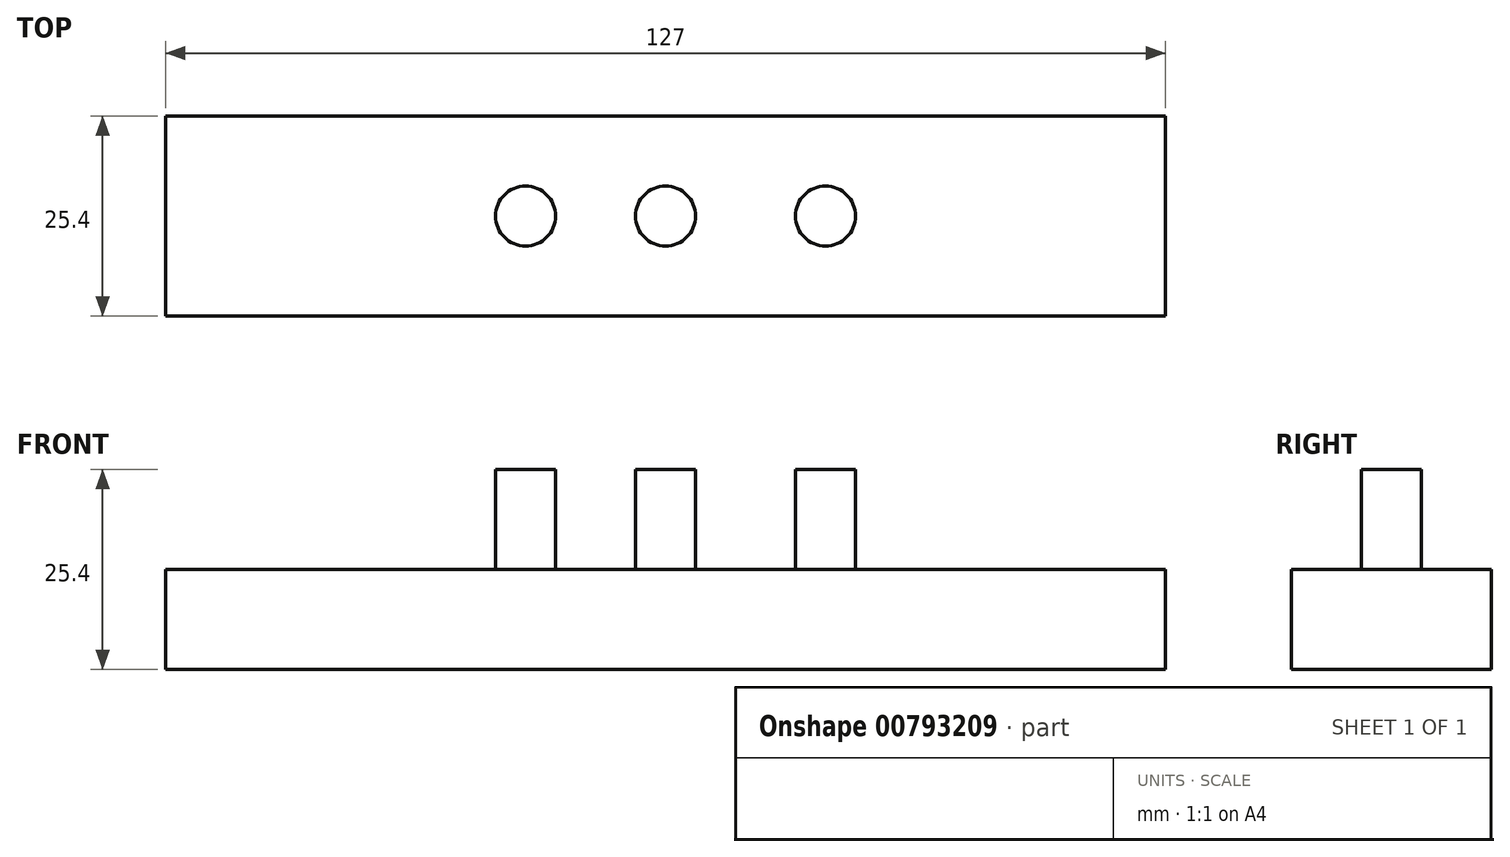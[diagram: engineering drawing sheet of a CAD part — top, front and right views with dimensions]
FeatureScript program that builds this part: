
annotation { "Feature Type Name" : "Feature", "Feature Type Description" : "" }
export const myFeature = defineFeature(function(context is Context, id is Id, definition is map)
    precondition{}
    {
        {
            var Q0;
            Q0=qCreatedBy(makeId("Top.planeOp"),FACE);
            var sketch = newSketch(context, id + "F0", { "sketchPlane" : qUnion([Q0])});
            skLineSegment(sketch, "E0.bottom", {"start": v(63.5, -12.7) * mm, "end": v(-63.5, -12.7) * mm});
            skLineSegment(sketch, "E0.top", {"start": v(63.5, 12.7) * mm, "end": v(-63.5, 12.7) * mm});
            skLineSegment(sketch, "E0.left", {"start": v(63.5, -12.7) * mm, "end": v(63.5, 12.7) * mm});
            skLineSegment(sketch, "E0.right", {"start": v(-63.5, -12.7) * mm, "end": v(-63.5, 12.7) * mm});
            skPoint(sketch, "E0.middle", {"position": v(0, 0) * mm});
            skSolve(sketch);
        }
        {
            var Q0;
            Q0=makeQuery(id+"F0.imprint","IMPRINT",FACE,{"disambiguationData":[TD([[makeQuery(id+"F0.imprint","IMPRINT",EDGE,{"derivedFrom":sQuery(id+"F0.wireOp",EDGE,"E0.bottom")}),-1.0]])]});
            extrude(context, id + "F1", {"entities" : qUnion([Q0]), "depth" : 12.7 * mm, "offsetDistance" : 25.4 * mm});
        }
        {
            var Q0;
            Q0=makeQuery(id+"F1.opExtrude","CAP_FACE",FACE,{"disambiguationData":[OSD([sQuery(id+"F0.wireOp",EDGE,"E0.bottom"),sQuery(id+"F0.wireOp",EDGE,"E0.top"),sQuery(id+"F0.wireOp",EDGE,"E0.left"),sQuery(id+"F0.wireOp",EDGE,"E0.right")])],"isStart":false});
            var sketch = newSketch(context, id + "F2", { "sketchPlane" : qUnion([Q0])});
            skCircle(sketch, "E1", {"center": v(-17.78, 0) * mm, "radius": 3.81 * mm});
            skCircle(sketch, "E2", {"center": v(0, 0) * mm, "radius": 3.81 * mm});
            skCircle(sketch, "E3", {"center": v(20.32, 0) * mm, "radius": 3.81 * mm});
            skSolve(sketch);
        }
        {
            var Q0;
            Q0 = qSketchRegion(id + "F2", true);
            extrude(context, id + "F3", {"entities" : qUnion([Q0]), "operationType" : NewBodyOperationType.ADD, "depth" : 12.7 * mm, "offsetDistance" : 25.4 * mm});
        }
    });
